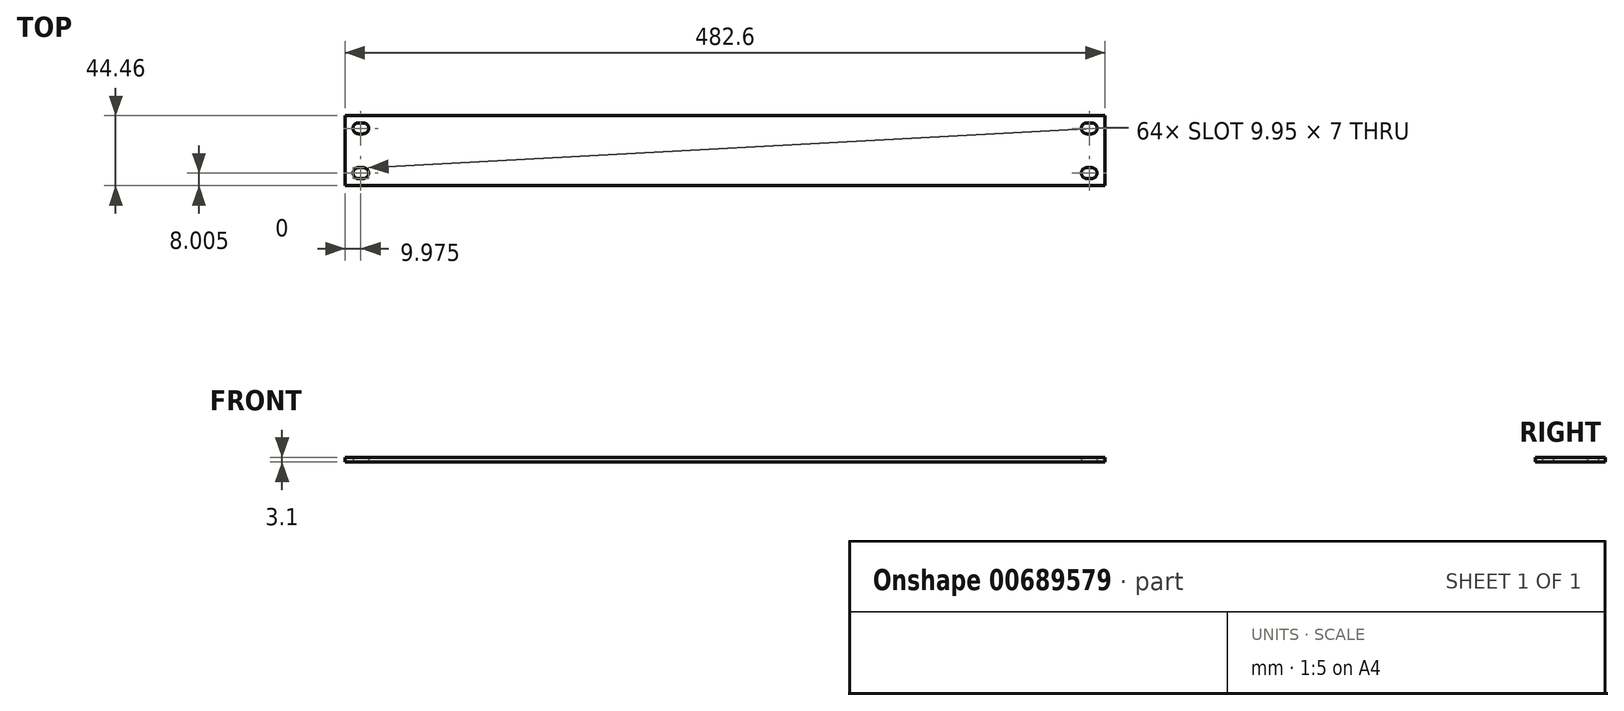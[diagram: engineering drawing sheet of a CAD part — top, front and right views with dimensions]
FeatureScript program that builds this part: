
annotation { "Feature Type Name" : "Feature", "Feature Type Description" : "" }
export const myFeature = defineFeature(function(context is Context, id is Id, definition is map)
    precondition{}
    {
        {
            var Q0;
            Q0=qCreatedBy(makeId("Top.planeOp"),FACE);
            var sketch = newSketch(context, id + "F0", { "sketchPlane" : qUnion([Q0])});
            skLineSegment(sketch, "E0.bottom", {"start": v(-241.3, -22.22) * mm, "end": v(241.3, -22.22) * mm});
            skLineSegment(sketch, "E0.top", {"start": v(-241.3, 22.22) * mm, "end": v(241.3, 22.22) * mm});
            skLineSegment(sketch, "E0.left", {"start": v(-241.3, -22.22) * mm, "end": v(-241.3, 22.22) * mm});
            skLineSegment(sketch, "E0.right", {"start": v(241.3, -22.22) * mm, "end": v(241.3, 22.22) * mm});
            skArc(sketch, "E1", {"start": v(-232.8, 17.73) * mm, "mid": v(-236.3, 14.23) * mm, "end": v(-232.8, 10.73) * mm});
            skArc(sketch, "E2", {"start": v(-229.85, 10.73) * mm, "mid": v(-226.35, 14.23) * mm, "end": v(-229.85, 17.73) * mm});
            skLineSegment(sketch, "E3", {"start": v(-232.8, 17.73) * mm, "end": v(-229.85, 17.73) * mm});
            skLineSegment(sketch, "E4", {"start": v(-232.8, 10.73) * mm, "end": v(-229.85, 10.73) * mm});
            skArc(sketch, "E5", {"start": v(-232.8, -10.72) * mm, "mid": v(-236.3, -14.22) * mm, "end": v(-232.8, -17.72) * mm});
            skArc(sketch, "E6", {"start": v(-229.85, -17.72) * mm, "mid": v(-226.35, -14.22) * mm, "end": v(-229.85, -10.72) * mm});
            skLineSegment(sketch, "E7", {"start": v(-232.8, -10.72) * mm, "end": v(-229.85, -10.72) * mm});
            skLineSegment(sketch, "E8", {"start": v(-232.8, -17.72) * mm, "end": v(-229.85, -17.72) * mm});
            skArc(sketch, "E9", {"start": v(229.85, 17.72) * mm, "mid": v(226.35, 14.22) * mm, "end": v(229.85, 10.72) * mm});
            skArc(sketch, "E10", {"start": v(232.8, 10.72) * mm, "mid": v(236.3, 14.22) * mm, "end": v(232.8, 17.72) * mm});
            skLineSegment(sketch, "E11", {"start": v(229.85, 17.72) * mm, "end": v(232.8, 17.72) * mm});
            skLineSegment(sketch, "E12", {"start": v(229.85, 10.72) * mm, "end": v(232.8, 10.72) * mm});
            skArc(sketch, "E13", {"start": v(229.85, -10.72) * mm, "mid": v(226.35, -14.22) * mm, "end": v(229.85, -17.72) * mm});
            skArc(sketch, "E14", {"start": v(232.8, -17.72) * mm, "mid": v(236.3, -14.22) * mm, "end": v(232.8, -10.72) * mm});
            skLineSegment(sketch, "E15", {"start": v(229.85, -10.72) * mm, "end": v(232.8, -10.72) * mm});
            skLineSegment(sketch, "E16", {"start": v(229.85, -17.72) * mm, "end": v(232.8, -17.72) * mm});
            skSolve(sketch);
        }
        {
            var Q0;
            Q0=makeQuery(id+"F0.imprint","IMPRINT",FACE,{"disambiguationData":[TD([[makeQuery(id+"F0.imprint","IMPRINT",EDGE,{"derivedFrom":sQuery(id+"F0.wireOp",EDGE,"E0.bottom")}),1.0]])]});
            extrude(context, id + "F1", {"entities" : qUnion([Q0]), "depth" : 3.1 * mm});
        }
    });
